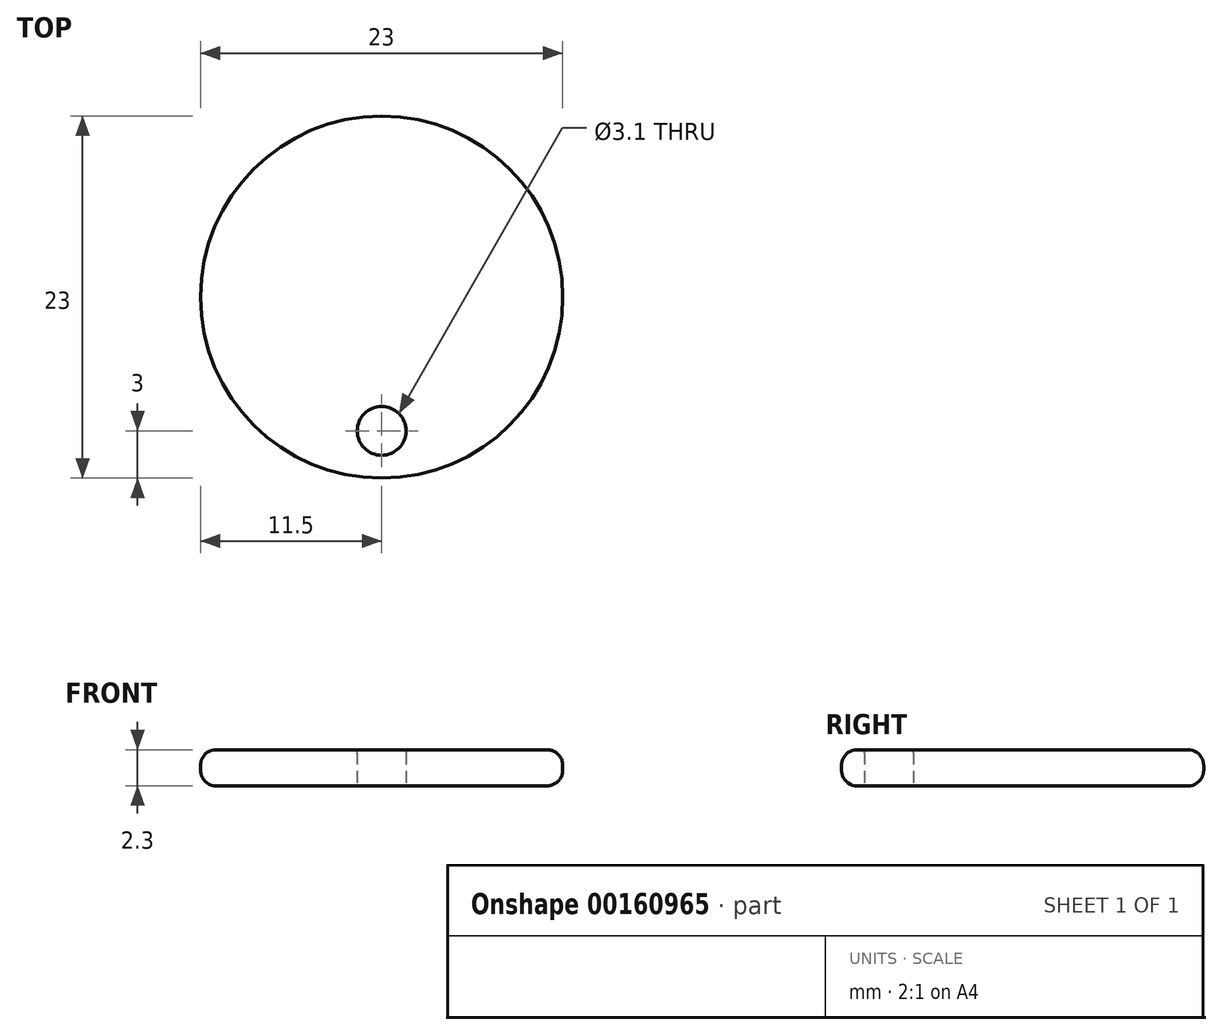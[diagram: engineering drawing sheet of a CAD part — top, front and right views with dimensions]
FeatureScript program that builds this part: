
annotation { "Feature Type Name" : "Feature", "Feature Type Description" : "" }
export const myFeature = defineFeature(function(context is Context, id is Id, definition is map)
    precondition{}
    {
        {
            var Q0;
            Q0=qCreatedBy(makeId("Top.planeOp"),FACE);
            var sketch = newSketch(context, id + "F0", { "sketchPlane" : qUnion([Q0])});
            skCircle(sketch, "E0", {"center": v(0, 0) * mm, "radius": 11.5 * mm});
            skSolve(sketch);
        }
        {
            var Q0;
            Q0=qCreatedBy(makeId("Top.planeOp"),FACE);
            var sketch = newSketch(context, id + "F1", { "sketchPlane" : qUnion([Q0])});
            skCircle(sketch, "E1", {"center": v(0, -8.5) * mm, "radius": 1.55 * mm});
            skSolve(sketch);
        }
        {
            var Q0;
            Q0 = qSketchRegion(id + "F0", true);
            extrude(context, id + "F2", {"entities" : qUnion([Q0]), "depth" : 2.3 * mm, "offsetDistance" : 25 * mm});
        }
        {
            var Q0;
            Q0 = qSketchRegion(id + "F1", true);
            extrude(context, id + "F3", {"entities" : qUnion([Q0]), "operationType" : NewBodyOperationType.REMOVE, "depth" : 25 * mm, "offsetDistance" : 25 * mm});
        }
        {
            var Q0;
            Q0=makeQuery(id+"F2.opExtrude","CAP_EDGE",EDGE,{"disambiguationData":[OSD([sQuery(id+"F0.wireOp",EDGE,"E0")])],"isStart":false});
            var Q1;
            Q1=makeQuery(id+"F2.opExtrude","CAP_EDGE",EDGE,{"disambiguationData":[OSD([sQuery(id+"F0.wireOp",EDGE,"E0")])],"isStart":true});
            fillet(context, id + "F4", {"entities" : qUnion([Q0, Q1]), "radius" : 1 * mm, "tangentPropagation" : true, "allowEdgeOverflow" : false});
        }
        {
            var Q0;
            Q0=makeQuery(id+"F3.boolean.opBoolean","INTERSECT",EDGE,{"derivedFrom":[makeQuery(id+"F2.opExtrude","CAP_FACE",FACE,{"disambiguationData":[OSD([sQuery(id+"F0.wireOp",EDGE,"E0")])],"isStart":false}),makeQuery(id+"F3.opExtrude","SWEPT_FACE",FACE,{"disambiguationData":[OSD([sQuery(id+"F1.wireOp",EDGE,"E1")])]})]});
            var Q1;
            Q1=makeQuery(id+"F3.boolean.opBoolean","COPY",EDGE,{"derivedFrom":makeQuery(id+"F3.opExtrude","CAP_EDGE",EDGE,{"disambiguationData":[OSD([sQuery(id+"F1.wireOp",EDGE,"E1")])],"isStart":true})});
            fillet(context, id + "F5", {"entities" : qUnion([Q0, Q1]), "radius" : 0.2 * mm, "tangentPropagation" : true, "allowEdgeOverflow" : false});
        }
    });
